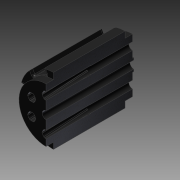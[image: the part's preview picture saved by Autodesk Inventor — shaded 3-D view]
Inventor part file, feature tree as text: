
AUTODESK INVENTOR PART (.ipt)
format: ipt  version: 2012 (Build 160160000, 160)  size: 768,000 bytes
history: native  units: mm
features: sketch x7, extrude x6, fillet x3, pattern_circular x2, other x1, helix x1
ambient origin geometry x8: Origin, YZ Plane, XZ Plane, XY Plane, X Axis, Y Axis, Z Axis, Center Point
bodies: Solid1 (feature_tree)
feature tree (20):
  extrude  "Extrusion1"  Depth=54.0mm
  extrude  "Extrusion2"  Depth=6.2mm
  sketch  "Sketch4"  dims[d15=100.0mm d16=0.0mm d17=13.5mm d18=1.0mm]
  other  "Work Axis1"
  helix  "Coil1"  [1 undecoded]
  pattern_circular  "Circular Pattern1"  Count=6 Angle=360.0deg
  extrude  "Extrusion3"  Depth=13.5mm
  fillet  "Fillet1"  Radius=1.0mm
  pattern_circular  "Circular Pattern2"  Count=6 Angle=360.0deg
  fillet  "Fillet2"  Radius=5.588mm
  extrude  "Extrusion4"  Depth=100.0mm TaperAngle=0.0deg
  extrude  "Extrusion5"  Depth=22.0mm
  extrude  "Extrusion6"  Depth=1.0mm
  fillet  "Fillet3"  Radius=60.0mm
  sketch  "Sketch2"  dims[d0=6.4mm d4=54.0mm]
  sketch  "Sketch3"  dims[d5=34.0mm d6=36.0mm d7=0.0mm d8=0.0mm d9=6.2mm d10=13.5mm d11=60.0mm d13=360.0deg]
  sketch  "Sketch5"  dims[d19=2.9mm d20=60.0mm d22=360.0deg d24=5.588mm]
  sketch  "Sketch6"  dims[d25=406.4mm d26=10.0mm d27=10.0mm d28=0.0mm d29=90.0deg d30=90.0deg d31=0.0mm d32=0.0mm d33=100.0mm d34=0.0mm d35=60.0mm d36=360.0deg]
  sketch  "Sketch7"  dims[d38=6.0mm d39=22.0mm]
  sketch  "Sketch8"  dims[d40=15.57mm d41=0.0mm d42=1.0mm d43=60.0mm d44=360.0deg d47=8.0mm d48=44.0mm d49=60.0mm d50=6.0mm d51=0.0mm d52=44.0mm d53=60.0mm d54=6.0mm d55=0.0mm d56=10.0mm d57=35.0mm d58=27.0mm d59=0.0mm d60=0.0mm d62=1.5mm d63=6.4mm]
note: 1 required parameter value undecoded (feature->parameter linkage not recoverable at this tier; creation-order binding heuristic only, values carry confidence <= 0.55)
